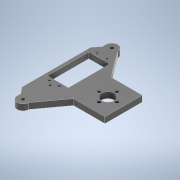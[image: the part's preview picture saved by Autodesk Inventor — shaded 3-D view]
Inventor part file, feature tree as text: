
AUTODESK INVENTOR PART (.ipt)
format: ipt  version: 2022 (Build 260153000, 153)  size: 150,528 bytes
history: native  units: mm
features: extrude x1, sketch x1
ambient origin geometry x8: Origin, YZ Plane, XZ Plane, XY Plane, X Axis, Y Axis, Z Axis, Center Point
bodies: Solid1 (feature_tree)
feature tree (2):
  extrude  "Extrusion1"  Depth=19.0mm
  sketch  "Sketch1"  dims[d0=19.0mm d1=19.0mm d2=90.0deg d3=32.0mm d4=68.5mm d5=35.0mm d8=13.0mm d10=3.5mm d18=10.75mm d22=2.5mm d28=40.0mm d30=360.0deg d35=12.0mm d39=6.0mm d40=0.0mm]
